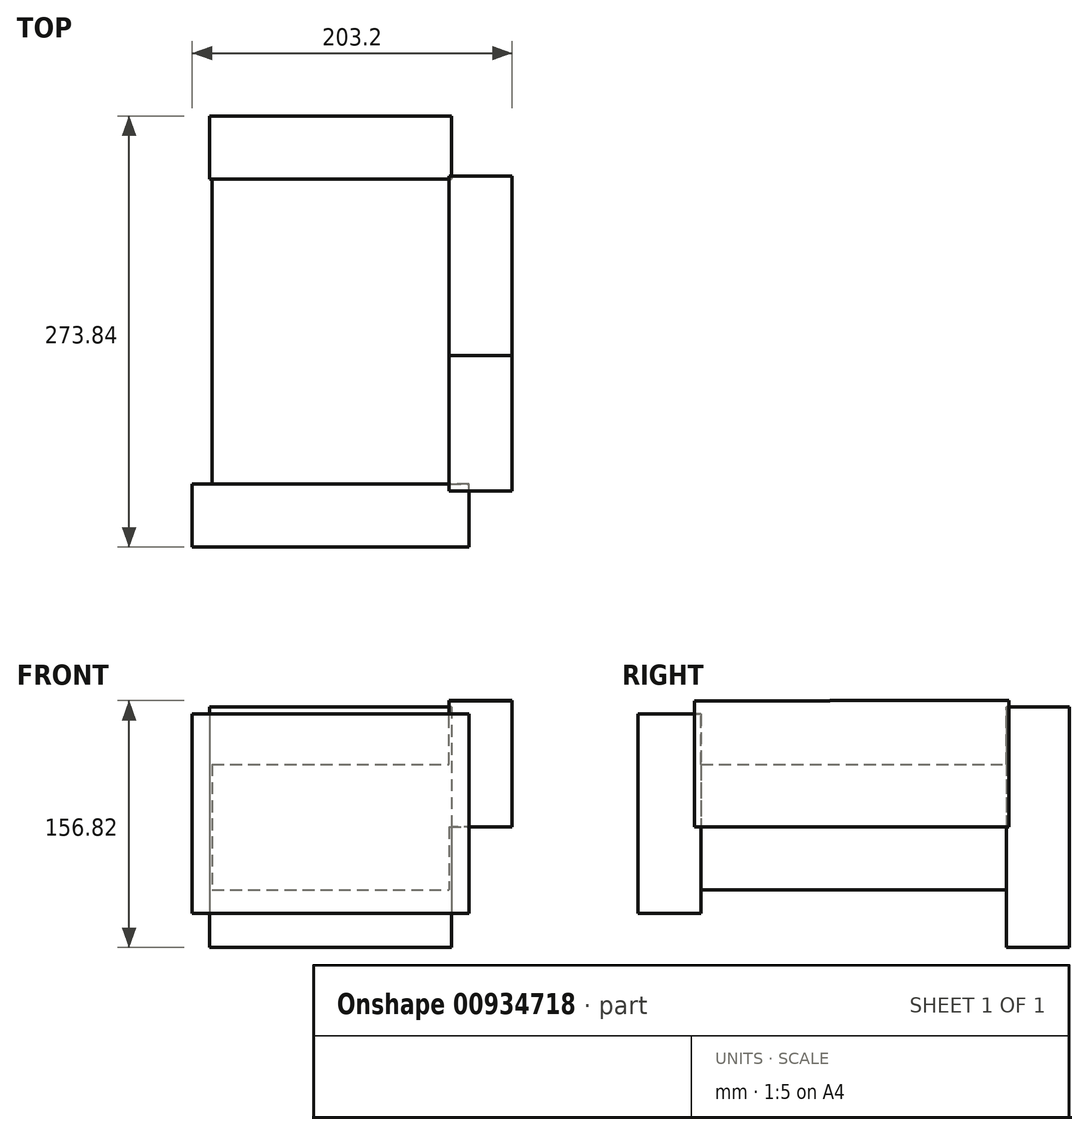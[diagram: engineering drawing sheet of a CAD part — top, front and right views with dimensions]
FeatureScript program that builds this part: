
annotation { "Feature Type Name" : "Feature", "Feature Type Description" : "" }
export const myFeature = defineFeature(function(context is Context, id is Id, definition is map)
    precondition{}
    {
        {
            var Q0;
            Q0=qCreatedBy(makeId("Top.planeOp"),FACE);
            var sketch = newSketch(context, id + "F0", { "sketchPlane" : qUnion([Q0])});
            skLineSegment(sketch, "E0.bottom", {"start": v(-75.28, -76.92) * mm, "end": v(75.28, -76.92) * mm});
            skLineSegment(sketch, "E0.top", {"start": v(-75.28, 76.92) * mm, "end": v(75.28, 76.92) * mm});
            skLineSegment(sketch, "E0.left", {"start": v(-75.28, -76.92) * mm, "end": v(-75.28, 76.92) * mm});
            skLineSegment(sketch, "E0.right", {"start": v(75.28, -76.92) * mm, "end": v(75.28, 76.92) * mm});
            skPoint(sketch, "E0.middle", {"position": v(0, 0) * mm});
            skSolve(sketch);
        }
        {
            var Q0;
            Q0 = qSketchRegion(id + "F0", true);
            extrude(context, id + "F1", {"entities" : qUnion([Q0]), "depth" : 40 * mm, "offsetDistance" : 25.4 * mm});
        }
        {
            var Q0;
            Q0=makeQuery(id+"F1.opExtrude","CAP_FACE",FACE,{"disambiguationData":[OSD([sQuery(id+"F0.wireOp",EDGE,"E0.bottom"),sQuery(id+"F0.wireOp",EDGE,"E0.top"),sQuery(id+"F0.wireOp",EDGE,"E0.left"),sQuery(id+"F0.wireOp",EDGE,"E0.right")])],"isStart":true});
            var sketch = newSketch(context, id + "F2", { "sketchPlane" : qUnion([Q0])});
            skLineSegment(sketch, "E1.bottom", {"start": v(-75.28, -76.92) * mm, "end": v(75.28, -76.92) * mm});
            skLineSegment(sketch, "E1.top", {"start": v(-75.28, 76.92) * mm, "end": v(75.28, 76.92) * mm});
            skLineSegment(sketch, "E1.left", {"start": v(-75.28, -76.92) * mm, "end": v(-75.28, 76.92) * mm});
            skLineSegment(sketch, "E1.right", {"start": v(75.28, -76.92) * mm, "end": v(75.28, 76.92) * mm});
            skPoint(sketch, "E1.middle", {"position": v(0, 0) * mm});
            skSolve(sketch);
        }
        {
            var Q0;
            Q0 = qSketchRegion(id + "F2", true);
            extrude(context, id + "F3", {"entities" : qUnion([Q0]), "operationType" : NewBodyOperationType.ADD, "depth" : 40 * mm, "offsetDistance" : 25.4 * mm});
        }
        {
            var Q0;
            Q0=makeQuery(id+"F3.boolean.opBoolean","MERGE",FACE,{"derivedFrom":[makeQuery(id+"F1.opExtrude","SWEPT_FACE",FACE,{"disambiguationData":[OSD([sQuery(id+"F0.wireOp",EDGE,"E0.top")])]}),makeQuery(id+"F3.opExtrude","SWEPT_FACE",FACE,{"disambiguationData":[OSD([sQuery(id+"F2.wireOp",EDGE,"E1.bottom")])]})]});
            var sketch = newSketch(context, id + "F4", { "sketchPlane" : qUnion([Q0])});
            skCircle(sketch, "E2", {"center": v(0, 0) * mm, "radius": 2.75 * mm});
            skSolve(sketch);
        }
        {
            var Q0;
            Q0=makeQuery(id+"F4.imprint","IMPRINT",FACE,{"disambiguationData":[TD([[makeQuery(id+"F4.imprint","IMPRINT",EDGE,{"derivedFrom":sQuery(id+"F4.wireOp",EDGE,"E2")}),1.0]])]});
            var Q1;
            Q1=makeQuery(id+"F4.imprint","IMPRINT",FACE,{"disambiguationData":[TD([[makeQuery(id+"F4.imprint","IMPRINT",EDGE,{"derivedFrom":sQuery(id+"F4.wireOp",EDGE,"E2")}),-1.0]])]});
            var Q2;
            Q2=makeQuery(id+"F3.boolean.opBoolean","MERGE",FACE,{"derivedFrom":[makeQuery(id+"F1.opExtrude","SWEPT_FACE",FACE,{"disambiguationData":[OSD([sQuery(id+"F0.wireOp",EDGE,"E0.top")])]}),makeQuery(id+"F3.opExtrude","SWEPT_FACE",FACE,{"disambiguationData":[OSD([sQuery(id+"F2.wireOp",EDGE,"E1.bottom")])]})]});
            var Q3;
            Q3=makeQuery(id+"F3.boolean.opBoolean","MERGE",FACE,{"derivedFrom":[makeQuery(id+"F1.opExtrude","SWEPT_FACE",FACE,{"disambiguationData":[OSD([sQuery(id+"F0.wireOp",EDGE,"E0.bottom")])]}),makeQuery(id+"F3.opExtrude","SWEPT_FACE",FACE,{"disambiguationData":[OSD([sQuery(id+"F2.wireOp",EDGE,"E1.top")])]})]});
            extrude(context, id + "F5", {"entities" : qUnion([Q0, Q1, Q2, Q3]), "operationType" : NewBodyOperationType.ADD, "depth" : 40 * mm, "offsetDistance" : 25.4 * mm});
        }
        {
            var Q0;
            Q0=makeQuery(id+"F3.boolean.opBoolean","MERGE",FACE,{"derivedFrom":[makeQuery(id+"F1.opExtrude","SWEPT_FACE",FACE,{"disambiguationData":[OSD([sQuery(id+"F0.wireOp",EDGE,"E0.bottom")])]}),makeQuery(id+"F3.opExtrude","SWEPT_FACE",FACE,{"disambiguationData":[OSD([sQuery(id+"F2.wireOp",EDGE,"E1.top")])]})]});
            var sketch = newSketch(context, id + "F6", { "sketchPlane" : qUnion([Q0])});
            skLineSegment(sketch, "E3.bottom", {"start": v(87.92, 71.8) * mm, "end": v(-87.92, 71.8) * mm});
            skLineSegment(sketch, "E3.top", {"start": v(87.92, -54.83) * mm, "end": v(-87.92, -54.83) * mm});
            skLineSegment(sketch, "E3.left", {"start": v(87.92, 71.8) * mm, "end": v(87.92, -54.83) * mm});
            skLineSegment(sketch, "E3.right", {"start": v(-87.92, 71.8) * mm, "end": v(-87.92, -54.83) * mm});
            skPoint(sketch, "E3.middle", {"position": v(0, 8.5) * mm});
            skSolve(sketch);
        }
        {
            var Q0;
            Q0 = qSketchRegion(id + "F6", true);
            extrude(context, id + "F7", {"entities" : qUnion([Q0]), "operationType" : NewBodyOperationType.ADD, "depth" : 40 * mm, "offsetDistance" : 25.4 * mm});
        }
        {
            var Q0;
            Q0=makeQuery(id+"F5.opExtrude","CAP_FACE",FACE,{"disambiguationData":[OSD([sQuery(id+"F0.wireOp",EDGE,"E0.top"),sQuery(id+"F2.wireOp",EDGE,"E1.bottom")])],"isStart":false});
            var sketch = newSketch(context, id + "F8", { "sketchPlane" : qUnion([Q0])});
            skLineSegment(sketch, "E4.bottom", {"start": v(-87.06, 72.38) * mm, "end": v(87.06, 72.38) * mm});
            skLineSegment(sketch, "E4.top", {"start": v(-87.06, -66.91) * mm, "end": v(87.06, -66.91) * mm});
            skLineSegment(sketch, "E4.left", {"start": v(-87.06, 72.38) * mm, "end": v(-87.06, -66.91) * mm});
            skLineSegment(sketch, "E4.right", {"start": v(87.06, 72.38) * mm, "end": v(87.06, -66.91) * mm});
            skPoint(sketch, "E4.middle", {"position": v(0, 2.73) * mm});
            skSolve(sketch);
        }
        {
            var Q0;
            {var subQ0=sQuery(id+"F2.wireOp",EDGE,"E1.right");var subQ1=sQuery(id+"F2.wireOp",EDGE,"E1.bottom");var subQ2=sQuery(id+"F0.wireOp",EDGE,"E0.right");var subQ3=sQuery(id+"F0.wireOp",EDGE,"E0.top");Q0=makeQuery(id+"F5.boolean.opBoolean","MERGE",FACE,{"derivedFrom":[makeQuery(id+"F3.boolean.opBoolean","MERGE",FACE,{"derivedFrom":[makeQuery(id+"F1.opExtrude","SWEPT_FACE",FACE,{"disambiguationData":[OSD([subQ2])]}),makeQuery(id+"F3.opExtrude","SWEPT_FACE",FACE,{"disambiguationData":[OSD([subQ0])]})]}),makeQuery(id+"F5.opExtrude","SWEPT_FACE",FACE,{"disambiguationData":[OSD([subQ3,subQ2,subQ1,subQ0]),TDD([makeQuery(id+"F3.boolean.opBoolean","MERGE",EDGE,{"derivedFrom":[makeQuery(id+"F1.opExtrude","SWEPT_EDGE",EDGE,{"disambiguationData":[OSD([subQ3,subQ2])]}),makeQuery(id+"F3.opExtrude","SWEPT_EDGE",EDGE,{"disambiguationData":[OSD([subQ1,subQ0])]})]})])]})]});}
            var sketch = newSketch(context, id + "F9", { "sketchPlane" : qUnion([Q0])});
            skLineSegment(sketch, "E5.bottom", {"start": v(4.9, 0) * mm, "end": v(-81.16, 0) * mm});
            skLineSegment(sketch, "E5.top", {"start": v(4.9, 80.15) * mm, "end": v(-81.16, 80.15) * mm});
            skLineSegment(sketch, "E5.left", {"start": v(4.9, 0) * mm, "end": v(4.9, 80.15) * mm});
            skLineSegment(sketch, "E5.right", {"start": v(-81.16, 0) * mm, "end": v(-81.16, 80.15) * mm});
            skSolve(sketch);
        }
        {
            var Q0;
            Q0 = qSketchRegion(id + "F9", true);
            extrude(context, id + "F10", {"entities" : qUnion([Q0]), "operationType" : NewBodyOperationType.ADD, "depth" : 40 * mm, "offsetDistance" : 25.4 * mm});
        }
        {
            var Q0;
            {var subQ0=sQuery(id+"F2.wireOp",EDGE,"E1.right");var subQ1=sQuery(id+"F2.wireOp",EDGE,"E1.bottom");var subQ2=sQuery(id+"F0.wireOp",EDGE,"E0.right");var subQ3=sQuery(id+"F0.wireOp",EDGE,"E0.top");Q0=makeQuery(id+"F5.boolean.opBoolean","MERGE",FACE,{"derivedFrom":[makeQuery(id+"F3.boolean.opBoolean","MERGE",FACE,{"derivedFrom":[makeQuery(id+"F1.opExtrude","SWEPT_FACE",FACE,{"disambiguationData":[OSD([subQ2])]}),makeQuery(id+"F3.opExtrude","SWEPT_FACE",FACE,{"disambiguationData":[OSD([subQ0])]})]}),makeQuery(id+"F5.opExtrude","SWEPT_FACE",FACE,{"disambiguationData":[OSD([subQ3,subQ2,subQ1,subQ0]),TDD([makeQuery(id+"F3.boolean.opBoolean","MERGE",EDGE,{"derivedFrom":[makeQuery(id+"F1.opExtrude","SWEPT_EDGE",EDGE,{"disambiguationData":[OSD([subQ3,subQ2])]}),makeQuery(id+"F3.opExtrude","SWEPT_EDGE",EDGE,{"disambiguationData":[OSD([subQ1,subQ0])]})]})])]})]});}
            var sketch = newSketch(context, id + "F11", { "sketchPlane" : qUnion([Q0])});
            skLineSegment(sketch, "E6.bottom", {"start": v(4.9, 0) * mm, "end": v(118.77, 0) * mm});
            skLineSegment(sketch, "E6.top", {"start": v(4.9, 80.37) * mm, "end": v(118.77, 80.37) * mm});
            skLineSegment(sketch, "E6.left", {"start": v(4.9, 0) * mm, "end": v(4.9, 80.37) * mm});
            skLineSegment(sketch, "E6.right", {"start": v(118.77, 0) * mm, "end": v(118.77, 80.37) * mm});
            skSolve(sketch);
        }
        {
            var Q0;
            Q0 = qSketchRegion(id + "F11", true);
            extrude(context, id + "F12", {"entities" : qUnion([Q0]), "operationType" : NewBodyOperationType.ADD, "depth" : 40 * mm, "offsetDistance" : 25.4 * mm});
        }
        {
            var Q0;
            {var subQ0=sQuery(id+"F0.wireOp",EDGE,"E0.top");Q0=makeQuery(id+"F8.imprint","IMPRINT",FACE,{"disambiguationData":[TD([[makeQuery(id+"F8.imprint","IMPRINT",EDGE,{"derivedFrom":makeQuery(id+"F5.opExtrude","CAP_EDGE",EDGE,{"disambiguationData":[OSD([subQ0]),TDD([makeQuery(id+"F1.opExtrude","CAP_EDGE",EDGE,{"disambiguationData":[OSD([subQ0])],"isStart":false})])],"isStart":false})}),1.0]])]});}
            var sketch = newSketch(context, id + "F13", { "sketchPlane" : qUnion([Q0])});
            skLineSegment(sketch, "E7.bottom", {"start": v(-76.8, 76.45) * mm, "end": v(76.8, 76.45) * mm});
            skLineSegment(sketch, "E7.top", {"start": v(-76.8, -76.45) * mm, "end": v(76.8, -76.45) * mm});
            skLineSegment(sketch, "E7.left", {"start": v(-76.8, 76.45) * mm, "end": v(-76.8, -76.45) * mm});
            skLineSegment(sketch, "E7.right", {"start": v(76.8, 76.45) * mm, "end": v(76.8, -76.45) * mm});
            skPoint(sketch, "E7.middle", {"position": v(0, 0) * mm});
            skSolve(sketch);
        }
        {
            var Q0;
            Q0 = qSketchRegion(id + "F13", true);
            extrude(context, id + "F14", {"entities" : qUnion([Q0]), "operationType" : NewBodyOperationType.ADD, "depth" : 40 * mm, "offsetDistance" : 25.4 * mm});
        }
    });
